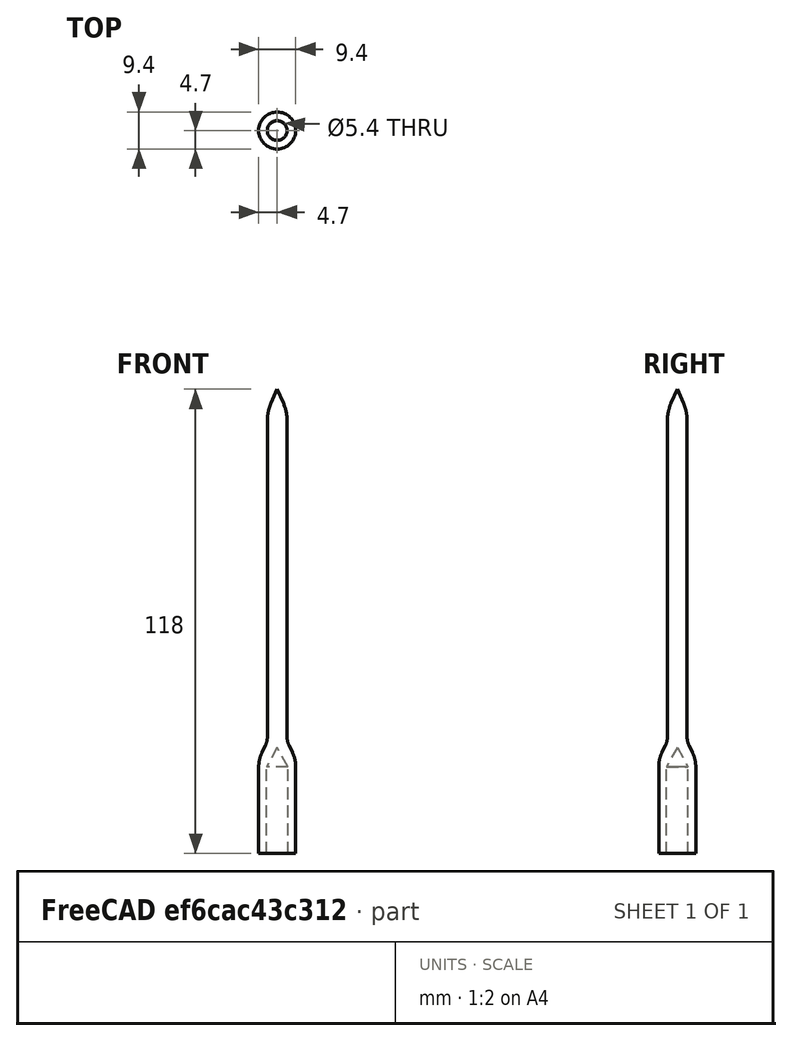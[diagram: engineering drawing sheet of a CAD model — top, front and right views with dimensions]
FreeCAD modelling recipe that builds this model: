
FCSTD DOCUMENT  (FreeCAD 0.15R4671 (Git))
Label: Claw5 - Calibration Pole
License: All rights reserved
LicenseURL: http://en.wikipedia.org/wiki/All_rights_reserved
objects: Sketcher::SketchObject×1, PartDesign::Revolution×1
note: 3 computed .brp shape members not serialized (recipe doc carries the construction recipe); baked Part::Feature solids carry a one-line shape summary decoded from their .brp

FEATURE [Sketcher::SketchObject] Sketch
  Placement = pos=(0,0,0) rot=(1,0,0;1.5708rad)
  sketch-geometry (11):
    g0: LineSegment StartX=2.7 StartY=0 StartZ=0 EndX=2.7 EndY=22 EndZ=0
    g1: LineSegment StartX=2.7 StartY=22 StartZ=0 EndX=0 EndY=27 EndZ=0
    g2: LineSegment StartX=0 StartY=27 StartZ=0 EndX=0 EndY=118 EndZ=0
    g3: LineSegment StartX=0 StartY=118 StartZ=0 EndX=1.57083 EndY=114.425 EndZ=0
    g4: LineSegment StartX=2.5 StartY=110 StartZ=0 EndX=2.5 EndY=29.6541 EndZ=0
    g5: LineSegment StartX=3.0067 StartY=27.4674 StartZ=0 EndX=3.83208 EndY=25.782 EndZ=0
    g6: LineSegment StartX=4.7 StartY=22.0364 StartZ=0 EndX=4.7 EndY=0 EndZ=0
    g7: LineSegment StartX=4.7 StartY=0 StartZ=0 EndX=2.7 EndY=0 EndZ=0
    g8: ArcOfCircle CenterX=-3.81645 CenterY=22.0364 CenterZ=0 NormalX=0 NormalY=0 NormalZ=1 Radius=8.51645 StartAngle=0 EndAngle=0.455393
    g9: ArcOfCircle CenterX=7.47191 CenterY=29.6541 CenterZ=0 NormalX=0 NormalY=0 NormalZ=1 Radius=4.97191 StartAngle=3.14159 EndAngle=3.59699
    g10: ArcOfCircle CenterX=-8.5 CenterY=110 CenterZ=0 NormalX=0 NormalY=0 NormalZ=1 Radius=11 StartAngle=0 EndAngle=0.413972
  constraints (26):
    c: PointOnObject(g0,g-1)
    c: Vertical(g0)
    c: Coincident(g0,g1)
    c: Coincident(g1,g2)
    c: Vertical(g2)
    c: Coincident(g2,g3)
    c: Vertical(g4)
    c: Vertical(g6)
    c: Coincident(g6,g7)
    c: Coincident(g7,g0)
    c: Horizontal(g7)
    c: DistanceX(g7) = -2
    c: DistanceX(g-1,g0) = 2.7
    c: PointOnObject(g1,g-2)
    c: DistanceY(g-1,g2) = 118
    c: Tangent(g5,g8) = 1.5708
    c: Tangent(g6,g8) = 1.5708
    c: Tangent(g5,g9) = -1.5708
    c: Tangent(g4,g9) = -1.5708
    c: Tangent(g3,g10) = 1.5708
    c: Tangent(g4,g10) = 1.5708
    c: DistanceX(g-1,g4) = 2.5
    c: DistanceY(g4,g2) = 8
    c: Radius(g10) = 11
    c: DistanceY(g-1,g0) = 22
    c: DistanceY(g1,g0) = -5
FEATURE [PartDesign::Revolution] Revolution
  Angle = 360
  Axis = (0,0,1)
  Base = (0,0,0)
  Placement = pos=(0,0,0) rot=(1,0,0;1.5708rad)
  ReferenceAxis = -> Sketch [V_Axis]
  Reversed = true
  Sketch = -> Sketch
